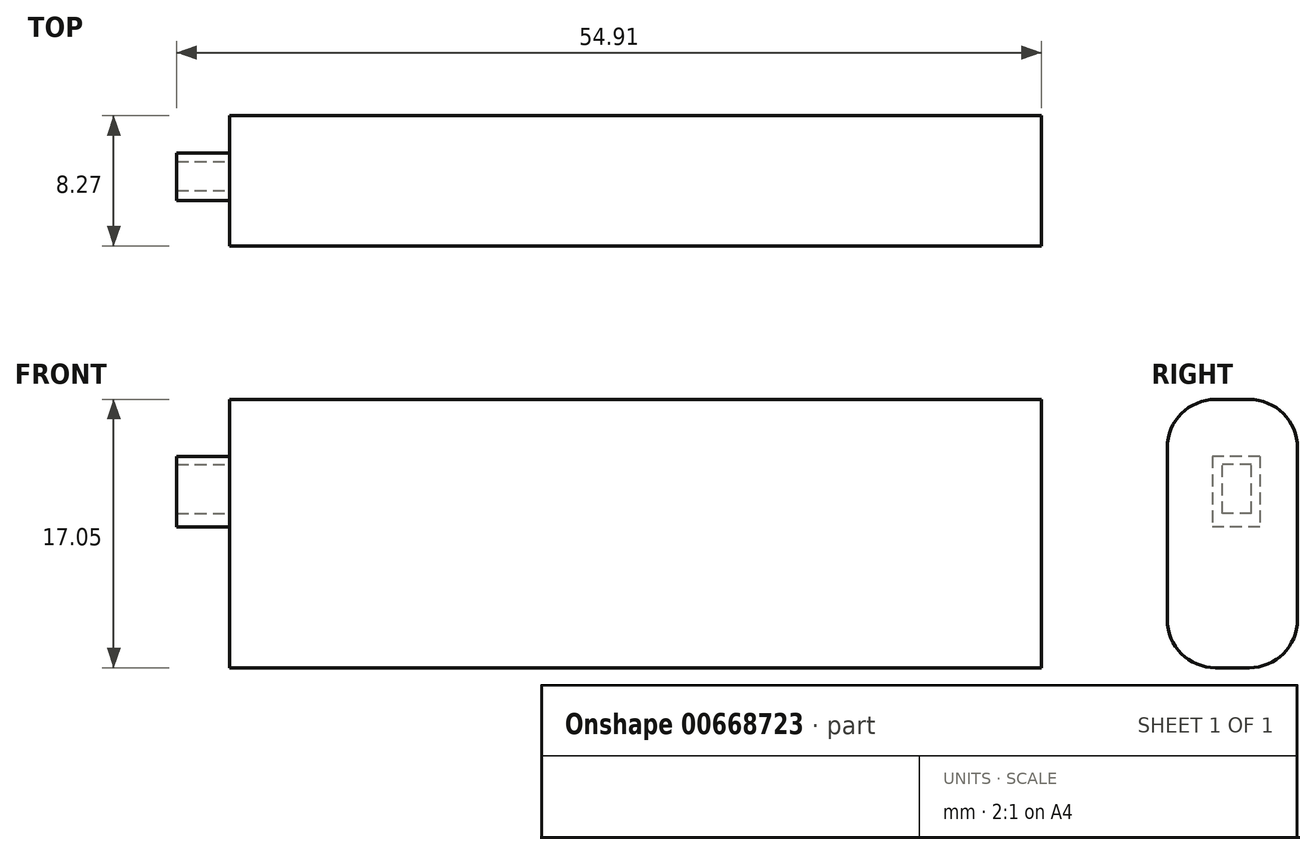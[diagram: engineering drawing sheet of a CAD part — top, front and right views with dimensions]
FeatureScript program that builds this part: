
annotation { "Feature Type Name" : "Feature", "Feature Type Description" : "" }
export const myFeature = defineFeature(function(context is Context, id is Id, definition is map)
    precondition{}
    {
        {
            var Q0;
            Q0=qCreatedBy(makeId("Right.planeOp"),FACE);
            var sketch = newSketch(context, id + "F0", { "sketchPlane" : qUnion([Q0])});
            skLineSegment(sketch, "E0.bottom", {"start": v(0, 0) * mm, "end": v(4.7, 0) * mm});
            skLineSegment(sketch, "E0.top", {"start": v(0, 17.05) * mm, "end": v(4.7, 17.05) * mm});
            skLineSegment(sketch, "E0.left", {"start": v(0, 0) * mm, "end": v(0, 17.05) * mm});
            skLineSegment(sketch, "E1.bottom", {"start": v(4.7, 17.05) * mm, "end": v(8.27, 17.05) * mm});
            skLineSegment(sketch, "E1.top", {"start": v(4.7, 0) * mm, "end": v(8.27, 0) * mm});
            skLineSegment(sketch, "E1.right", {"start": v(8.27, 17.05) * mm, "end": v(8.27, 0) * mm});
            skSolve(sketch);
        }
        {
            var Q0;
            Q0=makeQuery(id+"F0.imprint","IMPRINT",FACE,{"disambiguationData":[TD([[makeQuery(id+"F0.imprint","IMPRINT",EDGE,{"derivedFrom":sQuery(id+"F0.wireOp",EDGE,"E0.bottom")}),1.0]])]});
            extrude(context, id + "F1", {"entities" : qUnion([Q0]), "depth" : 51.56 * mm, "offsetDistance" : 25.4 * mm});
        }
        {
            var Q0;
            Q0=makeQuery(id+"F1.opExtrude","SWEPT_EDGE",EDGE,{"disambiguationData":[OSD([sQuery(id+"F0.wireOp",EDGE,"E1.bottom"),sQuery(id+"F0.wireOp",EDGE,"E1.right")])]});
            var Q1;
            Q1=makeQuery(id+"F1.opExtrude","SWEPT_EDGE",EDGE,{"disambiguationData":[OSD([sQuery(id+"F0.wireOp",EDGE,"E0.top"),sQuery(id+"F0.wireOp",EDGE,"E0.left")])]});
            var Q2;
            Q2=makeQuery(id+"F1.opExtrude","SWEPT_EDGE",EDGE,{"disambiguationData":[OSD([sQuery(id+"F0.wireOp",EDGE,"E1.top"),sQuery(id+"F0.wireOp",EDGE,"E1.right")])]});
            var Q3;
            Q3=makeQuery(id+"F1.opExtrude","SWEPT_EDGE",EDGE,{"disambiguationData":[OSD([sQuery(id+"F0.wireOp",EDGE,"E0.bottom"),sQuery(id+"F0.wireOp",EDGE,"E0.left")])]});
            fillet(context, id + "F2", {"entities" : qUnion([Q0, Q1, Q2, Q3]), "radius" : 3.07 * mm, "tangentPropagation" : true, "allowEdgeOverflow" : false});
        }
        {
            var Q0;
            Q0=qCreatedBy(makeId("Right.planeOp"),FACE);
            var sketch = newSketch(context, id + "F3", { "sketchPlane" : qUnion([Q0])});
            skLineSegment(sketch, "E2.bottom", {"start": v(5.9, 13.43) * mm, "end": v(2.88, 13.43) * mm});
            skLineSegment(sketch, "E2.top", {"start": v(5.9, 8.95) * mm, "end": v(2.88, 8.95) * mm});
            skLineSegment(sketch, "E2.left", {"start": v(5.9, 13.43) * mm, "end": v(5.9, 8.95) * mm});
            skLineSegment(sketch, "E2.right", {"start": v(2.88, 13.43) * mm, "end": v(2.88, 8.95) * mm});
            skLineSegment(sketch, "E3.bottom", {"start": v(5.35, 9.81) * mm, "end": v(3.5, 9.81) * mm});
            skLineSegment(sketch, "E3.top", {"start": v(5.35, 12.92) * mm, "end": v(3.5, 12.92) * mm});
            skLineSegment(sketch, "E3.left", {"start": v(5.35, 9.81) * mm, "end": v(5.35, 12.92) * mm});
            skLineSegment(sketch, "E3.right", {"start": v(3.5, 9.81) * mm, "end": v(3.5, 12.92) * mm});
            skSolve(sketch);
        }
        {
            var Q0;
            Q0=makeQuery(id+"F3.imprint","IMPRINT",FACE,{"disambiguationData":[TD([[makeQuery(id+"F3.imprint","IMPRINT",EDGE,{"derivedFrom":sQuery(id+"F3.wireOp",EDGE,"E2.bottom")}),1.0]])]});
            extrude(context, id + "F4", {"entities" : qUnion([Q0]), "operationType" : NewBodyOperationType.ADD, "oppositeDirection" : true, "depth" : 3.35 * mm, "offsetDistance" : 25.4 * mm});
        }
    });
